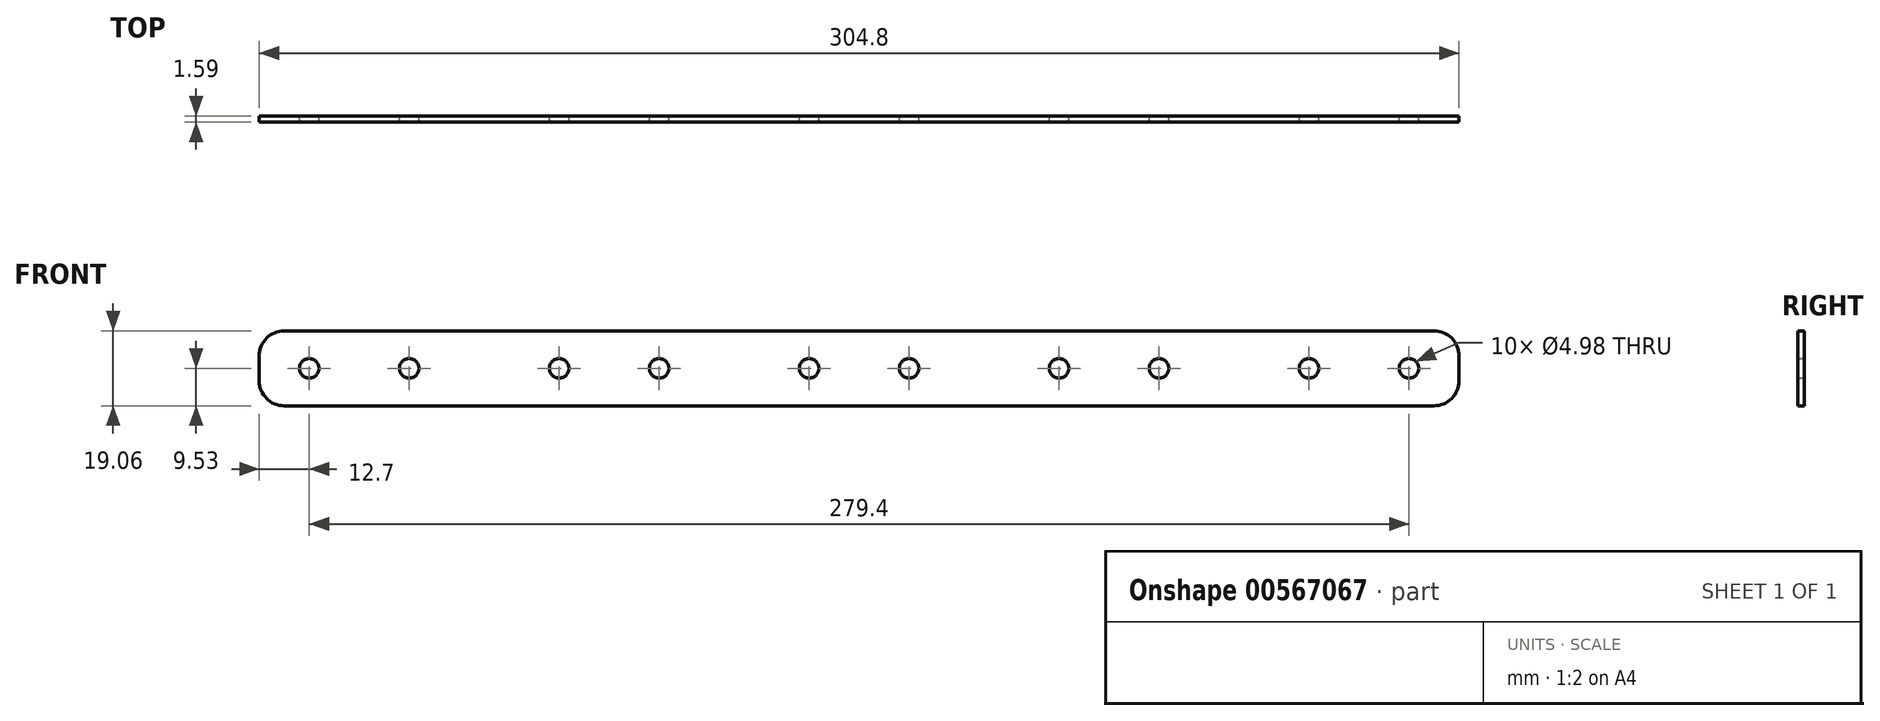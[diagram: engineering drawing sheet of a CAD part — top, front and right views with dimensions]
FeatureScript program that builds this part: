
annotation { "Feature Type Name" : "Feature", "Feature Type Description" : "" }
export const myFeature = defineFeature(function(context is Context, id is Id, definition is map)
    precondition{}
    {
        {
            var Q0;
            Q0=qCreatedBy(makeId("Front.planeOp"),FACE);
            var sketch = newSketch(context, id + "F0", { "sketchPlane" : qUnion([Q0])});
            skLineSegment(sketch, "E0.bottom", {"start": v(-146.05, 9.52) * mm, "end": v(146.05, 9.52) * mm});
            skLineSegment(sketch, "E0.top", {"start": v(-146.05, -9.53) * mm, "end": v(146.05, -9.53) * mm});
            skLineSegment(sketch, "E0.left", {"start": v(-152.4, 3.17) * mm, "end": v(-152.4, -3.18) * mm});
            skLineSegment(sketch, "E0.right", {"start": v(152.4, 3.17) * mm, "end": v(152.4, -3.18) * mm});
            skPoint(sketch, "E0.middle", {"position": v(0, 0) * mm});
            skCircle(sketch, "E1", {"center": v(-12.7, 0) * mm, "radius": 2.49 * mm});
            skCircle(sketch, "E2.MirrorC", {"center": v(12.7, 0) * mm, "radius": 2.49 * mm});
            skPoint(sketch, "E3.visualSharp", {"position": v(-152.4, 9.52) * mm});
            skArc(sketch, "E3.filletArc", {"start": v(-146.05, 9.52) * mm, "mid": v(-150.54, 7.67) * mm, "end": v(-152.4, 3.17) * mm});
            skPoint(sketch, "E4.visualSharp", {"position": v(-152.4, -9.53) * mm});
            skArc(sketch, "E4.filletArc", {"start": v(-152.4, -3.18) * mm, "mid": v(-150.54, -7.67) * mm, "end": v(-146.05, -9.53) * mm});
            skPoint(sketch, "E5.visualSharp", {"position": v(152.4, 9.52) * mm});
            skArc(sketch, "E5.filletArc", {"start": v(152.4, 3.17) * mm, "mid": v(150.54, 7.67) * mm, "end": v(146.05, 9.52) * mm});
            skPoint(sketch, "E6.visualSharp", {"position": v(152.4, -9.53) * mm});
            skArc(sketch, "E6.filletArc", {"start": v(146.05, -9.53) * mm, "mid": v(150.54, -7.67) * mm, "end": v(152.4, -3.18) * mm});
            skCircle(sketch, "E7.1.0.0", {"center": v(50.8, 0) * mm, "radius": 2.49 * mm});
            skCircle(sketch, "E7.1.0.1", {"center": v(76.2, 0) * mm, "radius": 2.49 * mm});
            skLineSegment(sketch, "E7.1.0.2", {"start": v(-82.55, -9.53) * mm, "end": v(209.55, -9.53) * mm});
            skCircle(sketch, "E7.2.0.0", {"center": v(114.3, 0) * mm, "radius": 2.49 * mm});
            skCircle(sketch, "E7.2.0.1", {"center": v(139.7, 0) * mm, "radius": 2.49 * mm});
            skLineSegment(sketch, "E7.2.0.2", {"start": v(-19.05, -9.53) * mm, "end": v(273.05, -9.53) * mm});
            skLineSegment(sketch, "E7.direction1", {"start": v(-12.7, 0) * mm, "end": v(50.8, 0) * mm, "construction": true});
            skCircle(sketch, "E8.MirrorC", {"center": v(-76.2, 0) * mm, "radius": 2.49 * mm});
            skCircle(sketch, "E9.MirrorC", {"center": v(-50.8, 0) * mm, "radius": 2.49 * mm});
            skCircle(sketch, "E10.MirrorC", {"center": v(-114.3, 0) * mm, "radius": 2.49 * mm});
            skCircle(sketch, "E11.MirrorC", {"center": v(-139.7, 0) * mm, "radius": 2.49 * mm});
            skSolve(sketch);
        }
        {
            var Q0;
            Q0=qSketchRegion(id+"F0",true);
            extrude(context, id + "F1", {"entities" : qUnion([Q0]), "depth" : 1.59 * mm});
        }
    });
